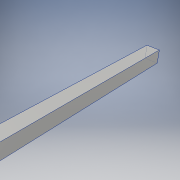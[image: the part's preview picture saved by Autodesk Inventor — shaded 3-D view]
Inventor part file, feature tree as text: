
AUTODESK INVENTOR PART (.ipt)
format: ipt  version: 2019 (Build 230136000, 136)  size: 95,232 bytes
history: native  units: in
note: dims shown in document units (in); Inventor stores cm internally (conversion verified against a paired STEP export)
features: extrude x1, sketch x1
ambient origin geometry x8: Origin, YZ Plane, XZ Plane, XY Plane, X Axis, Y Axis, Z Axis, Center Point
bodies: Solid1 (feature_tree)
feature tree (2):
  extrude  "Extrusion1"  Depth=12.0in TaperAngle=0.0deg
  sketch  "Sketch1"  dims[d0=1.0in d1=12.0in d2=0.0in]
